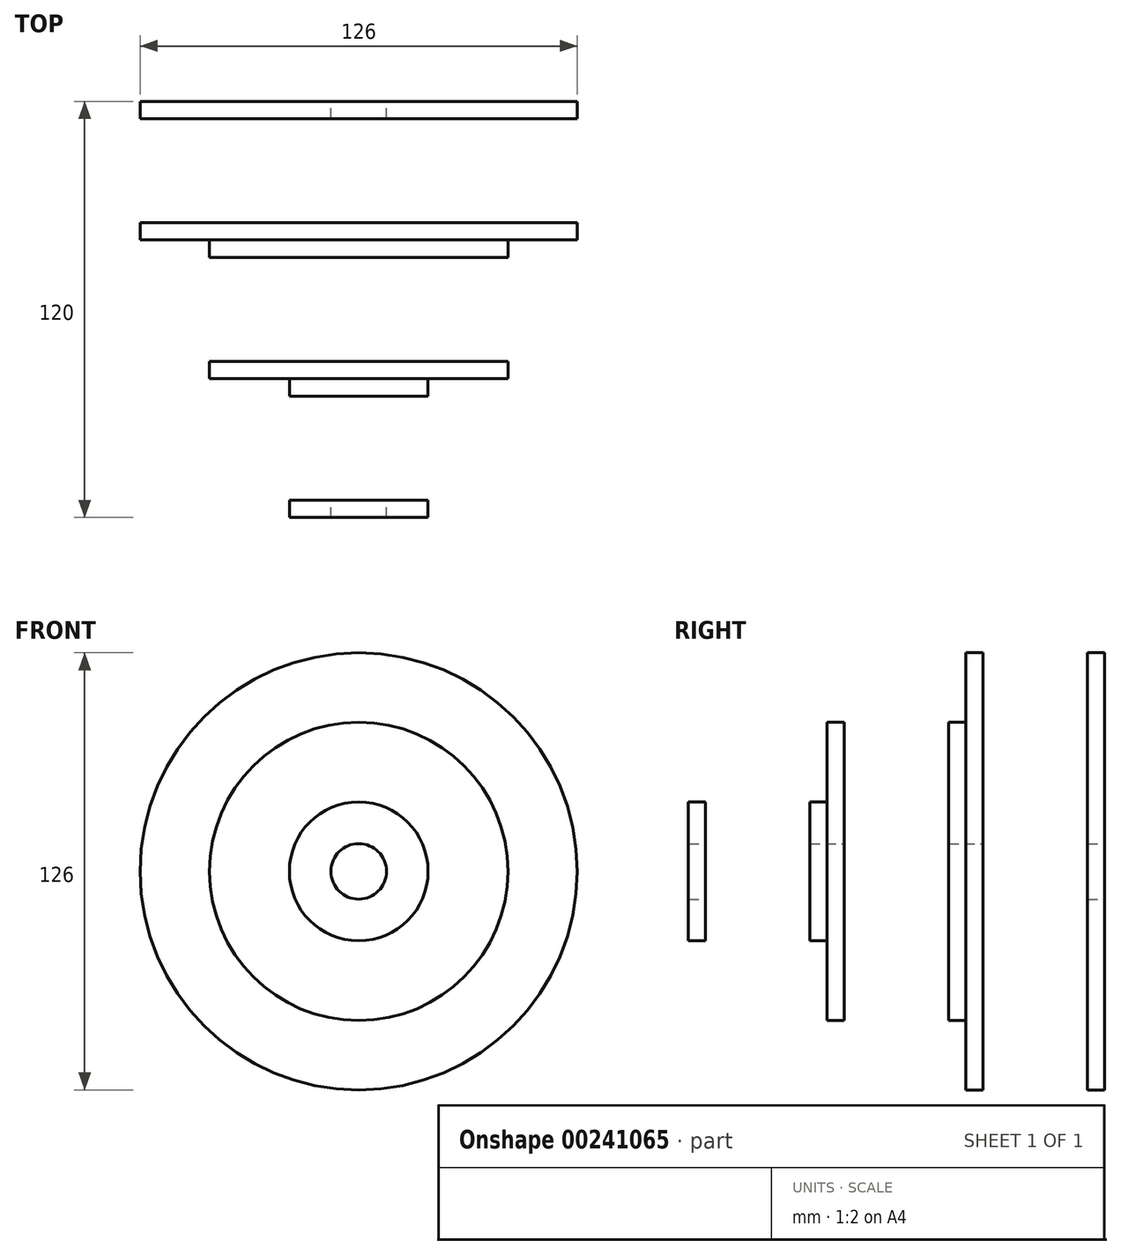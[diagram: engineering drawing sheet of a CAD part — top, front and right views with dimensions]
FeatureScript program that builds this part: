
annotation { "Feature Type Name" : "Feature", "Feature Type Description" : "" }
export const myFeature = defineFeature(function(context is Context, id is Id, definition is map)
    precondition{}
    {
        {
            var Q0;
            Q0=qCreatedBy(makeId("Right.planeOp"),FACE);
            var sketch = newSketch(context, id + "F0", { "sketchPlane" : qUnion([Q0])});
            skLineSegment(sketch, "E0", {"start": v(15, 60) * mm, "end": v(15, 0) * mm});
            skLineSegment(sketch, "E1", {"start": v(45, 60) * mm, "end": v(45, 0) * mm});
            skLineSegment(sketch, "E2", {"start": v(45, 0) * mm, "end": v(15, 0) * mm});
            skArc(sketch, "E3", {"start": v(15, 60) * mm, "mid": v(30, 55.03) * mm, "end": v(45, 60) * mm});
            skLineSegment(sketch, "E4.bottom", {"start": v(15, 0) * mm, "end": v(10, 0) * mm});
            skLineSegment(sketch, "E4.top", {"start": v(15, 63) * mm, "end": v(10, 63) * mm});
            skLineSegment(sketch, "E4.left", {"start": v(15, 0) * mm, "end": v(15, 63) * mm});
            skLineSegment(sketch, "E4.right", {"start": v(10, 0) * mm, "end": v(10, 63) * mm});
            skLineSegment(sketch, "E5", {"start": v(30, -14.2) * mm, "end": v(30, -32.48) * mm, "construction": true});
            skPoint(sketch, "E5.startSnap0", {"position": v(30, 0) * mm});
            skLineSegment(sketch, "E6.MirrorCS", {"start": v(45, 0) * mm, "end": v(50, 0) * mm});
            skLineSegment(sketch, "E7.MirrorCS", {"start": v(50, 0) * mm, "end": v(50, 63) * mm});
            skLineSegment(sketch, "E8.MirrorCS", {"start": v(45, 63) * mm, "end": v(50, 63) * mm});
            skLineSegment(sketch, "E9.MirrorCS", {"start": v(45, 0) * mm, "end": v(45, 63) * mm});
            skLineSegment(sketch, "E10.bottom", {"start": v(50, 0) * mm, "end": v(55, 0) * mm});
            skLineSegment(sketch, "E10.top", {"start": v(50, 43) * mm, "end": v(55, 43) * mm});
            skLineSegment(sketch, "E10.left", {"start": v(50, 0) * mm, "end": v(50, 43) * mm});
            skLineSegment(sketch, "E10.right", {"start": v(55, 0) * mm, "end": v(55, 43) * mm});
            skLineSegment(sketch, "E11", {"start": v(55, 0) * mm, "end": v(85, 0) * mm});
            skPoint(sketch, "E12.oppositeSnap0", {"position": v(52.5, 43) * mm});
            skLineSegment(sketch, "E12.bottom", {"start": v(85, 0) * mm, "end": v(90, 0) * mm});
            skLineSegment(sketch, "E12.top", {"start": v(85, 43) * mm, "end": v(90, 43) * mm});
            skLineSegment(sketch, "E12.left", {"start": v(85, 0) * mm, "end": v(85, 43) * mm});
            skLineSegment(sketch, "E12.right", {"start": v(90, 0) * mm, "end": v(90, 43) * mm});
            skPoint(sketch, "E13", {"position": v(55, 40) * mm});
            skPoint(sketch, "E14", {"position": v(85, 40) * mm});
            skArc(sketch, "E15", {"start": v(55, 40) * mm, "mid": v(70, 35.03) * mm, "end": v(85, 40) * mm});
            skLineSegment(sketch, "E16.bottom", {"start": v(90, 0) * mm, "end": v(95, 0) * mm});
            skLineSegment(sketch, "E16.top", {"start": v(90, 20) * mm, "end": v(95, 20) * mm});
            skLineSegment(sketch, "E16.left", {"start": v(90, 0) * mm, "end": v(90, 20) * mm});
            skLineSegment(sketch, "E16.right", {"start": v(95, 0) * mm, "end": v(95, 20) * mm});
            skLineSegment(sketch, "E17", {"start": v(95, 0) * mm, "end": v(125, 0) * mm});
            skLineSegment(sketch, "E18.bottom", {"start": v(125, 0) * mm, "end": v(130, 0) * mm});
            skLineSegment(sketch, "E18.top", {"start": v(125, 20) * mm, "end": v(130, 20) * mm});
            skLineSegment(sketch, "E18.left", {"start": v(125, 0) * mm, "end": v(125, 20) * mm});
            skLineSegment(sketch, "E18.right", {"start": v(130, 0) * mm, "end": v(130, 20) * mm});
            skPoint(sketch, "E19", {"position": v(95, 17) * mm});
            skPoint(sketch, "E20", {"position": v(125, 17) * mm});
            skArc(sketch, "E21", {"start": v(95, 17) * mm, "mid": v(110, 12.03) * mm, "end": v(125, 17) * mm});
            skLineSegment(sketch, "E22", {"start": v(10, 8) * mm, "end": v(130, 8) * mm});
            skPoint(sketch, "E23", {"position": v(-10, -27.12) * mm});
            skLineSegment(sketch, "E24", {"start": v(0, -7.65) * mm, "end": v(0, -67.77) * mm, "construction": true});
            skLineSegment(sketch, "E25.MirrorCS", {"start": v(-45, 0) * mm, "end": v(-50, 0) * mm});
            skLineSegment(sketch, "E26.MirrorCS", {"start": v(-85, 0) * mm, "end": v(-90, 0) * mm});
            skLineSegment(sketch, "E27.MirrorCS", {"start": v(-50, 0) * mm, "end": v(-55, 0) * mm});
            skLineSegment(sketch, "E28.MirrorCS", {"start": v(-50, 43) * mm, "end": v(-55, 43) * mm});
            skLineSegment(sketch, "E29.MirrorCS", {"start": v(-90, 0) * mm, "end": v(-95, 0) * mm});
            skLineSegment(sketch, "E30.MirrorCS", {"start": v(-125, 20) * mm, "end": v(-130, 20) * mm});
            skLineSegment(sketch, "E31.MirrorCS", {"start": v(-15, 0) * mm, "end": v(-10, 0) * mm});
            skLineSegment(sketch, "E32.MirrorCS", {"start": v(-45, 63) * mm, "end": v(-50, 63) * mm});
            skLineSegment(sketch, "E33.MirrorCS", {"start": v(-15, 63) * mm, "end": v(-10, 63) * mm});
            skLineSegment(sketch, "E34.MirrorCS", {"start": v(-125, 0) * mm, "end": v(-130, 0) * mm});
            skLineSegment(sketch, "E35.MirrorCS", {"start": v(-85, 43) * mm, "end": v(-90, 43) * mm});
            skLineSegment(sketch, "E36.MirrorCS", {"start": v(-90, 20) * mm, "end": v(-95, 20) * mm});
            skLineSegment(sketch, "E37.MirrorCS", {"start": v(-15, 60) * mm, "end": v(-15, 0) * mm});
            skLineSegment(sketch, "E38.MirrorCS", {"start": v(-45, 60) * mm, "end": v(-45, 0) * mm});
            skLineSegment(sketch, "E39.MirrorCS", {"start": v(-130, 0) * mm, "end": v(-130, 20) * mm});
            skLineSegment(sketch, "E40.MirrorCS", {"start": v(-50, 0) * mm, "end": v(-50, 43) * mm});
            skLineSegment(sketch, "E41.MirrorCS", {"start": v(-45, 0) * mm, "end": v(-45, 63) * mm});
            skLineSegment(sketch, "E42.MirrorCS", {"start": v(-90, 0) * mm, "end": v(-90, 20) * mm});
            skLineSegment(sketch, "E43.MirrorCS", {"start": v(-95, 0) * mm, "end": v(-95, 20) * mm});
            skLineSegment(sketch, "E44.MirrorCS", {"start": v(-15, 0) * mm, "end": v(-15, 63) * mm});
            skLineSegment(sketch, "E45.MirrorCS", {"start": v(-45, 0) * mm, "end": v(-15, 0) * mm});
            skPoint(sketch, "E46.MirrorP", {"position": v(-30, 0) * mm});
            skPoint(sketch, "E47.MirrorP", {"position": v(-95, 17) * mm});
            skArc(sketch, "E48.MirrorCS", {"start": v(-55, 40) * mm, "mid": v(-70, 35.03) * mm, "end": v(-85, 40) * mm});
            skLineSegment(sketch, "E49.MirrorCS", {"start": v(-85, 0) * mm, "end": v(-85, 43) * mm});
            skLineSegment(sketch, "E50.MirrorCS", {"start": v(-10, 8) * mm, "end": v(-130, 8) * mm});
            skLineSegment(sketch, "E51.MirrorCS", {"start": v(-95, 0) * mm, "end": v(-125, 0) * mm});
            skArc(sketch, "E52.MirrorCS", {"start": v(-95, 17) * mm, "mid": v(-110, 12.03) * mm, "end": v(-125, 17) * mm});
            skPoint(sketch, "E53.MirrorP", {"position": v(-55, 40) * mm});
            skLineSegment(sketch, "E54.MirrorCS", {"start": v(-125, 0) * mm, "end": v(-125, 20) * mm});
            skPoint(sketch, "E55.MirrorP", {"position": v(-52.5, 43) * mm});
            skArc(sketch, "E56.MirrorCS", {"start": v(-15, 60) * mm, "mid": v(-30, 55.03) * mm, "end": v(-45, 60) * mm});
            skLineSegment(sketch, "E57.MirrorCS", {"start": v(-10, 0) * mm, "end": v(-10, 63) * mm});
            skLineSegment(sketch, "E58.MirrorCS", {"start": v(-50, 0) * mm, "end": v(-50, 63) * mm});
            skPoint(sketch, "E59.MirrorP", {"position": v(-125, 17) * mm});
            skPoint(sketch, "E60.MirrorP", {"position": v(-85, 40) * mm});
            skLineSegment(sketch, "E61.MirrorCS", {"start": v(-55, 0) * mm, "end": v(-55, 43) * mm});
            skLineSegment(sketch, "E62.MirrorCS", {"start": v(-55, 0) * mm, "end": v(-85, 0) * mm});
            skLineSegment(sketch, "E63.MirrorCS", {"start": v(-90, 0) * mm, "end": v(-90, 43) * mm});
            skSolve(sketch);
        }
        {
            var Q0;
            {var subQ6=sQuery(id+"F0.wireOp",EDGE,"E33.MirrorCS");Q0=makeQuery(id+"F0.imprint","IMPRINT",FACE,{"disambiguationData":[TD([[makeQuery(id+"F0.imprint","IMPRINT",EDGE,{"derivedFrom":subQ6}),-1.0]])]});}
            var Q1;
            {var subQ0=sQuery(id+"F0.wireOp",EDGE,"E56.MirrorCS");Q1=makeQuery(id+"F0.imprint","IMPRINT",FACE,{"disambiguationData":[TD([[makeQuery(id+"F0.imprint","IMPRINT",EDGE,{"derivedFrom":subQ0}),1.0]])]});}
            var Q2;
            {var subQ5=sQuery(id+"F0.wireOp",EDGE,"E32.MirrorCS");Q2=makeQuery(id+"F0.imprint","IMPRINT",FACE,{"disambiguationData":[TD([[makeQuery(id+"F0.imprint","IMPRINT",EDGE,{"derivedFrom":subQ5}),1.0]])]});}
            var Q3;
            {var subQ1=sQuery(id+"F0.wireOp",EDGE,"E28.MirrorCS");Q3=makeQuery(id+"F0.imprint","IMPRINT",FACE,{"disambiguationData":[TD([[makeQuery(id+"F0.imprint","IMPRINT",EDGE,{"derivedFrom":subQ1}),1.0]])]});}
            var Q4;
            {var subQ0=sQuery(id+"F0.wireOp",EDGE,"E48.MirrorCS");Q4=makeQuery(id+"F0.imprint","IMPRINT",FACE,{"disambiguationData":[TD([[makeQuery(id+"F0.imprint","IMPRINT",EDGE,{"derivedFrom":subQ0}),1.0]])]});}
            var Q5;
            {var subQ6=sQuery(id+"F0.wireOp",EDGE,"E35.MirrorCS");Q5=makeQuery(id+"F0.imprint","IMPRINT",FACE,{"disambiguationData":[TD([[makeQuery(id+"F0.imprint","IMPRINT",EDGE,{"derivedFrom":subQ6}),1.0]])]});}
            var Q6;
            {var subQ5=sQuery(id+"F0.wireOp",EDGE,"E36.MirrorCS");Q6=makeQuery(id+"F0.imprint","IMPRINT",FACE,{"disambiguationData":[TD([[makeQuery(id+"F0.imprint","IMPRINT",EDGE,{"derivedFrom":subQ5}),1.0]])]});}
            var Q7;
            {var subQ0=sQuery(id+"F0.wireOp",EDGE,"E52.MirrorCS");Q7=makeQuery(id+"F0.imprint","IMPRINT",FACE,{"disambiguationData":[TD([[makeQuery(id+"F0.imprint","IMPRINT",EDGE,{"derivedFrom":subQ0}),1.0]])]});}
            var Q8;
            {var subQ6=sQuery(id+"F0.wireOp",EDGE,"E30.MirrorCS");Q8=makeQuery(id+"F0.imprint","IMPRINT",FACE,{"disambiguationData":[TD([[makeQuery(id+"F0.imprint","IMPRINT",EDGE,{"derivedFrom":subQ6}),1.0]])]});}
            var Q9;
            Q9=sQuery(id+"F0.wireOp",EDGE,"E2");
            revolve(context, id + "F1", {"entities" : qUnion([Q0, Q1, Q2, Q3, Q4, Q5, Q6, Q7, Q8]), "axis" : qUnion([Q9]), "revolveType" : RevolveType.FULL});
        }
        {
            var Q0;
            Q0=qCreatedBy(makeId("Top.planeOp"),FACE);
            var sketch = newSketch(context, id + "F2", { "sketchPlane" : qUnion([Q0])});
            skLineSegment(sketch, "E64", {"start": v(140, -136.09) * mm, "end": v(140, 119.23) * mm, "construction": true});
            skSolve(sketch);
        }
        {
            var Q0;
            Q0=sQuery(id+"F2.wireOp",EDGE,"E64");
            var Q1;
            Q1=qCreatedBy(makeId("Right.planeOp"),FACE);
            cPlane(context, id + "F3", {"entities" : qUnion([Q0, Q1]), "cplaneType" : CPlaneType.LINE_ANGLE, "offset" : 25 * mm, "angle" : 0 * degree, "width" : 150 * mm, "height" : 150 * mm});
        }
        {
            var Q0;
            Q0=qCreatedBy(makeId("Top.planeOp"),FACE);
            var sketch = newSketch(context, id + "F4", { "sketchPlane" : qUnion([Q0])});
            skLineSegment(sketch, "E65.bottom", {"start": v(140, -140.02) * mm, "end": v(0, -140.02) * mm});
            skLineSegment(sketch, "E65.top", {"start": v(140, -195.2) * mm, "end": v(0, -195.2) * mm});
            skLineSegment(sketch, "E65.left", {"start": v(140, -140.02) * mm, "end": v(140, -195.2) * mm});
            skLineSegment(sketch, "E65.right", {"start": v(0, -140.02) * mm, "end": v(0, -195.2) * mm});
            skSolve(sketch);
        }
    });
